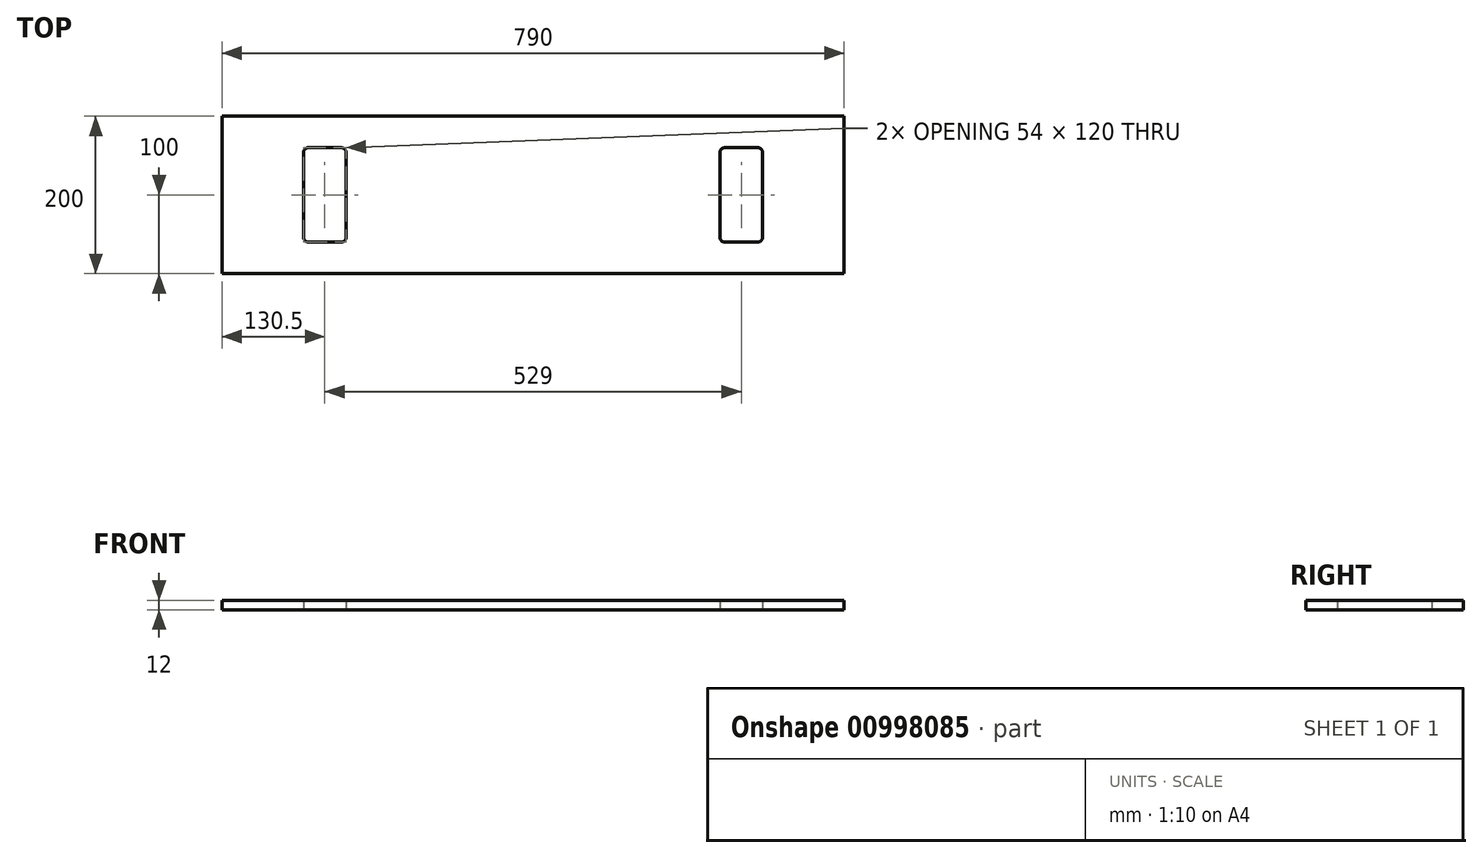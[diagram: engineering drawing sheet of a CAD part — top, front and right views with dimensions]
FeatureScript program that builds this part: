
annotation { "Feature Type Name" : "Feature", "Feature Type Description" : "" }
export const myFeature = defineFeature(function(context is Context, id is Id, definition is map)
    precondition{}
    {
        {
            var Q0;
            Q0=qCreatedBy(makeId("Top.planeOp"),FACE);
            var sketch = newSketch(context, id + "F0", { "sketchPlane" : qUnion([Q0])});
            skLineSegment(sketch, "E0", {"start": v(0, 100) * mm, "end": v(395, 100) * mm});
            skLineSegment(sketch, "E1", {"start": v(395, 100) * mm, "end": v(395, -100) * mm});
            skLineSegment(sketch, "E2", {"start": v(395, -100) * mm, "end": v(0, -100) * mm});
            skLineSegment(sketch, "E3.bottom", {"start": v(243.5, 60) * mm, "end": v(285.5, 60) * mm});
            skLineSegment(sketch, "E3.top", {"start": v(243.5, -60) * mm, "end": v(285.5, -60) * mm});
            skLineSegment(sketch, "E3.left", {"start": v(237.5, 54) * mm, "end": v(237.5, -54) * mm});
            skLineSegment(sketch, "E3.right", {"start": v(291.5, 54) * mm, "end": v(291.5, -54) * mm});
            skPoint(sketch, "E4.visualSharp", {"position": v(237.5, 60) * mm});
            skArc(sketch, "E4.filletArc", {"start": v(243.5, 60) * mm, "mid": v(239.26, 58.24) * mm, "end": v(237.5, 54) * mm});
            skPoint(sketch, "E5.visualSharp", {"position": v(291.5, 60) * mm});
            skArc(sketch, "E5.filletArc", {"start": v(291.5, 54) * mm, "mid": v(289.74, 58.24) * mm, "end": v(285.5, 60) * mm});
            skPoint(sketch, "E6.visualSharp", {"position": v(291.5, -60) * mm});
            skArc(sketch, "E6.filletArc", {"start": v(285.5, -60) * mm, "mid": v(289.74, -58.24) * mm, "end": v(291.5, -54) * mm});
            skPoint(sketch, "E7.visualSharp", {"position": v(237.5, -60) * mm});
            skArc(sketch, "E7.filletArc", {"start": v(237.5, -54) * mm, "mid": v(239.26, -58.24) * mm, "end": v(243.5, -60) * mm});
            skArc(sketch, "E8.MirrorCS", {"start": v(-243.5, 60) * mm, "mid": v(-239.26, 58.24) * mm, "end": v(-237.5, 54) * mm});
            skArc(sketch, "E9.MirrorCS", {"start": v(-291.5, 54) * mm, "mid": v(-289.74, 58.24) * mm, "end": v(-285.5, 60) * mm});
            skArc(sketch, "E10.MirrorCS", {"start": v(-237.5, -54) * mm, "mid": v(-239.26, -58.24) * mm, "end": v(-243.5, -60) * mm});
            skArc(sketch, "E11.MirrorCS", {"start": v(-285.5, -60) * mm, "mid": v(-289.74, -58.24) * mm, "end": v(-291.5, -54) * mm});
            skLineSegment(sketch, "E12.MirrorCS", {"start": v(-237.5, 54) * mm, "end": v(-237.5, -54) * mm});
            skPoint(sketch, "E13.MirrorP", {"position": v(-237.5, 60) * mm});
            skLineSegment(sketch, "E14.MirrorCS", {"start": v(-291.5, 54) * mm, "end": v(-291.5, -54) * mm});
            skLineSegment(sketch, "E15.MirrorCS", {"start": v(0, 100) * mm, "end": v(-395, 100) * mm});
            skPoint(sketch, "E16.MirrorP", {"position": v(-237.5, -60) * mm});
            skLineSegment(sketch, "E17.MirrorCS", {"start": v(-243.5, 60) * mm, "end": v(-285.5, 60) * mm});
            skLineSegment(sketch, "E18.MirrorCS", {"start": v(-243.5, -60) * mm, "end": v(-285.5, -60) * mm});
            skLineSegment(sketch, "E19.MirrorCS", {"start": v(-395, 100) * mm, "end": v(-395, -100) * mm});
            skLineSegment(sketch, "E20.MirrorCS", {"start": v(-395, -100) * mm, "end": v(0, -100) * mm});
            skPoint(sketch, "E21.MirrorP", {"position": v(-291.5, 60) * mm});
            skPoint(sketch, "E22.MirrorP", {"position": v(-291.5, -60) * mm});
            skSolve(sketch);
        }
        {
            var Q0;
            Q0 = qSketchRegion(id + "F0", true);
            extrude(context, id + "F1", {"entities" : qUnion([Q0]), "depth" : 12 * mm, "offsetDistance" : 25 * mm});
        }
    });
